# Revit family: Клапан надлишкового тиску КНТК_Ukr
name_source: partatom
category: Mechanical Equipment
units: mm (PartAtom-declared; Revit-internal decimal feet)

## family parameters
Always vertical = Yes
Cut with Voids When Loaded = No
OmniClass Number = 23.75.00.00
OmniClass Title = Climate Control (HVAC)
Part Type = Normal
Room Calculation Point = No
Round Connector Dimension = Use Diameter
Shared = No
Work Plane-Based = No

## types (5) — shared parameters
00_20_Виробник = Вентс
00_20_Назва = Клапан надлишкового тиску КНТК
Матеріал зони обслуговуваня = <By Category>
zero-valued in all types: Default Elevation

## per-type parameters (varying)
| type | D | D1 | D2 | H | L | R1 | d | Вага | Матеріал корпусу |
| КНТК-100 | 100 mm  [stored 0.328084 ft] | 200 mm  [stored 0.656168 ft] | 224 mm  [stored 0.734908 ft] | 168 mm | 325 mm  [stored 1.06627 ft] | 50 mm  [stored 0.164042 ft] | 12 mm  [stored 0.0393701 ft] | 3.60 kg | Вуглецева сталь з порошковим покриттям RAL 5007 Muar |
| КНТК-150 | 150 mm | 238 mm | 262 mm | 168 mm | 368 mm | 75 mm | 12 mm  [stored 0.0393701 ft] | 4.10 kg | <By Category> |
| КНТК-200 | 200 mm  [stored 0.656168 ft] | 285 mm  [stored 0.935039 ft] | 309 mm  [stored 1.01378 ft] | 167 mm | 443 mm | 100 mm  [stored 0.328084 ft] | 14 mm  [stored 0.0459318 ft] | 5.50 kg | <By Category> |
| КНТК-250 | 250 mm  [stored 0.82021 ft] | 325 mm  [stored 1.06627 ft] | 349 mm  [stored 1.14501 ft] | 167 mm | 521 mm  [stored 1.70932 ft] | 125 mm  [stored 0.410105 ft] | 14 mm  [stored 0.0459318 ft] | 6.60 kg | <By Category> |
| КНТК-300 | 300 mm | 430 mm | 454 mm  [stored 1.4895 ft] | 202 mm | 595 mm  [stored 1.9521 ft] | 150 mm | 14 mm  [stored 0.0459318 ft] | 7.80 kg | <By Category> |

note: column(s) folded — value = type name in every type: 00_20_Тип

note: [stored X ft] marks values corroborated as IEEE doubles in the binary element streams (Revit-internal decimal feet)

## geometry (parser evidence)
native form markers: Sweep x6
no freeform markers — native parametric forms only
